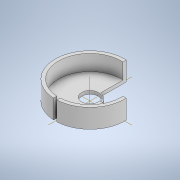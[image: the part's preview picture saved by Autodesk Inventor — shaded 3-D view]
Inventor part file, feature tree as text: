
AUTODESK INVENTOR PART (.ipt)
format: ipt  version: 2022 (Build 260153000, 153)  size: 178,176 bytes
history: native  units: in
note: dims shown in document units (in); Inventor stores cm internally (conversion verified against a paired STEP export)
features: extrude x2, sketch x2, chamfer x1
ambient origin geometry x8: Origin, YZ Plane, XZ Plane, XY Plane, X Axis, Y Axis, Z Axis, Center Point
bodies: Body1 (feature_tree)
feature tree (5):
  extrude  "Extrusion5"  Depth=0.0394in
  chamfer  "Chamfer1"  Distance=0.0394in
  extrude  "Extrusion8"  Depth=0.0787in
  sketch  "Sketch9"  dims[d30=1.6535in d31=0.0394in]
  sketch  "Sketch12"  dims[d32=0.0394in d33=0.0394in d34=0.0394in d35=0.3937in d36=0.0787in d37=0.0in d38=0.4724in d39=0.0197in d40=0.0394in d41=45.0deg d42=0.0787in d50=0.0787in d53=1.4961in d58=1.6535in d60=0.748in d61=0.4528in d62=0.0in d63=0.0787in d64=0.0787in d65=0.0787in d66=0.0787in d23=0.5in d24=0.0344in d25=0.5in d26=0.0344in d43=0.0in d44=0.0in d45=0.0in]
